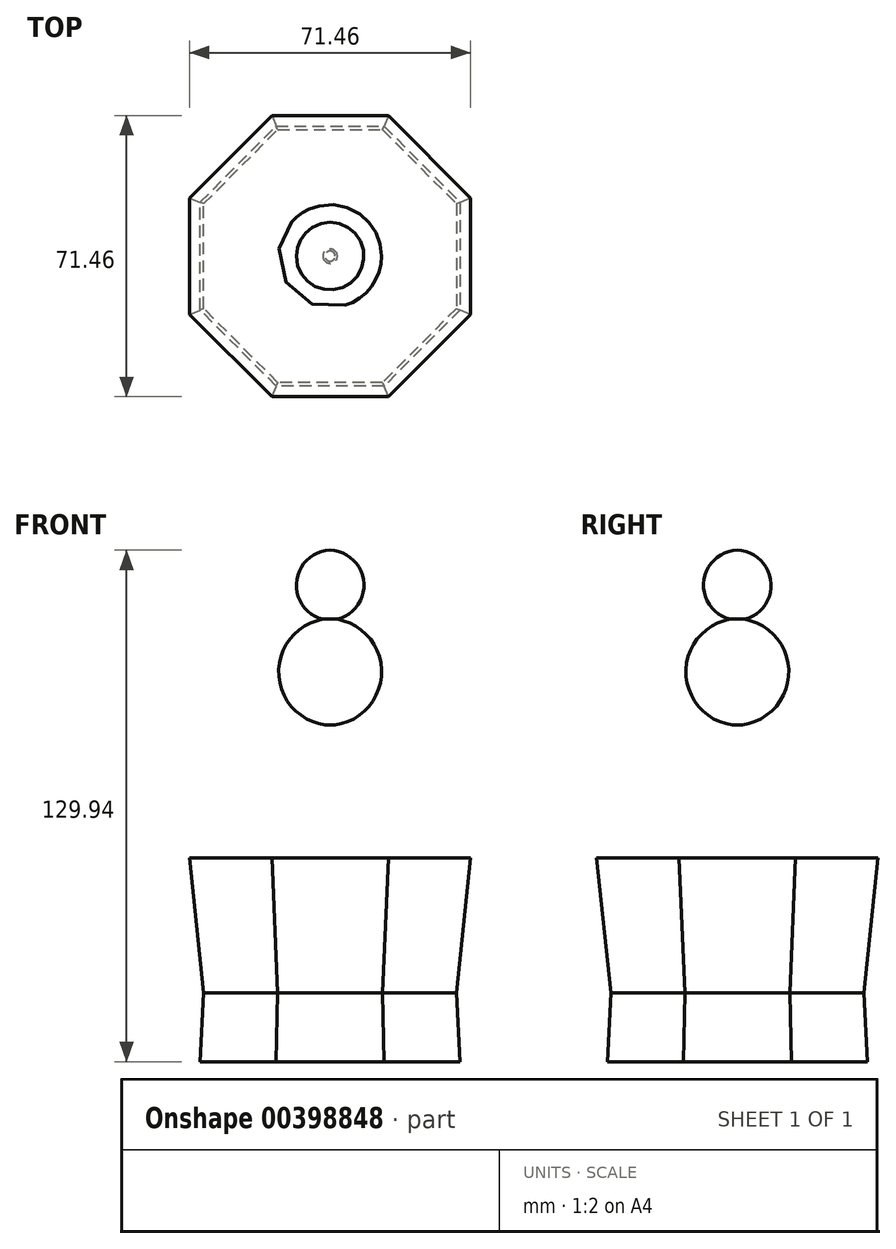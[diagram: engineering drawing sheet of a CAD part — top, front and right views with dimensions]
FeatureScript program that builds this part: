
annotation { "Feature Type Name" : "Feature", "Feature Type Description" : "" }
export const myFeature = defineFeature(function(context is Context, id is Id, definition is map)
    precondition{}
    {
        {
            var Q0;
            Q0=qCreatedBy(makeId("Top.planeOp"),FACE);
            var sketch = newSketch(context, id + "F0", { "sketchPlane" : qUnion([Q0])});
            skCircle(sketch, "E0.cCircle", {"center": v(0, 0) * mm, "radius": 32.12 * mm, "construction": true});
            skLineSegment(sketch, "E0.0", {"start": v(-13.3, 32.12) * mm, "end": v(13.3, 32.12) * mm});
            skLineSegment(sketch, "E0.1", {"start": v(13.3, 32.12) * mm, "end": v(32.12, 13.3) * mm});
            skLineSegment(sketch, "E0.2", {"start": v(32.12, 13.3) * mm, "end": v(32.12, -13.3) * mm});
            skLineSegment(sketch, "E0.3", {"start": v(32.12, -13.3) * mm, "end": v(13.3, -32.12) * mm});
            skLineSegment(sketch, "E0.4", {"start": v(13.3, -32.12) * mm, "end": v(-13.3, -32.12) * mm});
            skLineSegment(sketch, "E0.5", {"start": v(-13.3, -32.12) * mm, "end": v(-32.12, -13.3) * mm});
            skLineSegment(sketch, "E0.6", {"start": v(-32.12, -13.3) * mm, "end": v(-32.12, 13.3) * mm});
            skLineSegment(sketch, "E0.7", {"start": v(-32.12, 13.3) * mm, "end": v(-13.3, 32.12) * mm});
            skPoint(sketch, "E0.0.midPoint", {"position": v(0, 32.12) * mm});
            skSolve(sketch);
        }
        {
            var Q0;
            Q0=makeQuery(id+"F0.imprint","IMPRINT",FACE,{"disambiguationData":[TD([[makeQuery(id+"F0.imprint","IMPRINT",EDGE,{"derivedFrom":sQuery(id+"F0.wireOp",EDGE,"E0.0")}),-1.0]])]});
            extrude(context, id + "F1", {"entities" : qUnion([Q0]), "depth" : 34.3 * mm, "hasDraft" : true, "draftAngle" : 6 * degree, "hasSecondDirection" : true, "secondDirectionOppositeDirection" : true, "secondDirectionDepth" : 17.53 * mm, "hasSecondDirectionDraft" : true, "secondDirectionDraftAngle" : 3 * degree});
        }
        {
            var Q0;
            Q0=qCreatedBy(makeId("Front.planeOp"),FACE);
            var sketch = newSketch(context, id + "F2", { "sketchPlane" : qUnion([Q0])});
            skLineSegment(sketch, "E1", {"start": v(0, 76.07) * mm, "end": v(0, 0) * mm});
            skArc(sketch, "E2", {"start": v(0, 67.99) * mm, "mid": v(-6.96, 36.33) * mm, "end": v(8.47, 64.84) * mm});
            skSolve(sketch);
        }
        {
            var Q0;
            {var subQ0=sQuery(id+"F2.wireOp",EDGE,"E2");var subQ1=sQuery(id+"F2.wireOp",EDGE,"E1");var subQ2=makeQuery(id+"F2.imprint","INTERSECT",VERTEX,{"disambiguationData":[OD(0.0)],"derivedFrom":[subQ1,subQ0]});Q0=makeQuery(id+"F2.imprint","IMPRINT",FACE,{"disambiguationData":[TD([[makeQuery(id+"F2.imprint","IMPRINT",EDGE,{"disambiguationData":[TD([[subQ2,-1.0]])],"derivedFrom":subQ1}),-1.0]])]});}
            var Q1;
            Q1=sQuery(id+"F2.wireOp",EDGE,"E1");
            revolve(context, id + "F3", {"entities" : qUnion([Q0]), "axis" : qUnion([Q1]), "revolveType" : RevolveType.FULL});
        }
        {
            var Q0;
            Q0=qCreatedBy(makeId("Front.planeOp"),FACE);
            var sketch = newSketch(context, id + "F4", { "sketchPlane" : qUnion([Q0])});
            skLineSegment(sketch, "E3", {"start": v(0, 104.37) * mm, "end": v(0, 0) * mm});
            skLineSegment(sketch, "E4", {"start": v(0, 10.57) * mm, "end": v(0, 0) * mm});
            skArc(sketch, "E5", {"start": v(0, 95.09) * mm, "mid": v(-4.2, 68.76) * mm, "end": v(9.81, 91.44) * mm});
            skSolve(sketch);
        }
        {
            var Q0;
            {var subQ0=sQuery(id+"F4.wireOp",EDGE,"E5");var subQ1=sQuery(id+"F4.wireOp",EDGE,"E3");var subQ2=makeQuery(id+"F4.imprint","INTERSECT",VERTEX,{"disambiguationData":[OD(0.0)],"derivedFrom":[subQ1,subQ0]});Q0=makeQuery(id+"F4.imprint","IMPRINT",FACE,{"disambiguationData":[TD([[makeQuery(id+"F4.imprint","IMPRINT",EDGE,{"disambiguationData":[TD([[subQ2,-1.0]])],"derivedFrom":subQ1}),-1.0]])]});}
            var Q1;
            Q1=sQuery(id+"F4.wireOp",EDGE,"E3");
            revolve(context, id + "F5", {"operationType" : NewBodyOperationType.ADD, "entities" : qUnion([Q0]), "axis" : qUnion([Q1]), "revolveType" : RevolveType.FULL});
        }
        {
            var Q0;
            Q0=qCreatedBy(makeId("Front.planeOp"),FACE);
            var sketch = newSketch(context, id + "F6", { "sketchPlane" : qUnion([Q0])});
            skLineSegment(sketch, "E6", {"start": v(0, 125.52) * mm, "end": v(0, 0) * mm});
            skArc(sketch, "E7", {"start": v(0, 112.41) * mm, "mid": v(-2.59, 95.1) * mm, "end": v(6.04, 110.33) * mm});
            skSolve(sketch);
        }
        {
            var Q0;
            {var subQ0=sQuery(id+"F6.wireOp",EDGE,"E7");var subQ1=sQuery(id+"F6.wireOp",EDGE,"E6");var subQ2=makeQuery(id+"F6.imprint","INTERSECT",VERTEX,{"disambiguationData":[OD(0.0)],"derivedFrom":[subQ1,subQ0]});Q0=makeQuery(id+"F6.imprint","IMPRINT",FACE,{"disambiguationData":[TD([[makeQuery(id+"F6.imprint","IMPRINT",EDGE,{"disambiguationData":[TD([[subQ2,-1.0]])],"derivedFrom":subQ1}),-1.0]])]});}
            var Q1;
            Q1=sQuery(id+"F6.wireOp",EDGE,"E6");
            revolve(context, id + "F7", {"operationType" : NewBodyOperationType.ADD, "entities" : qUnion([Q0]), "axis" : qUnion([Q1]), "revolveType" : RevolveType.FULL});
        }
    });
